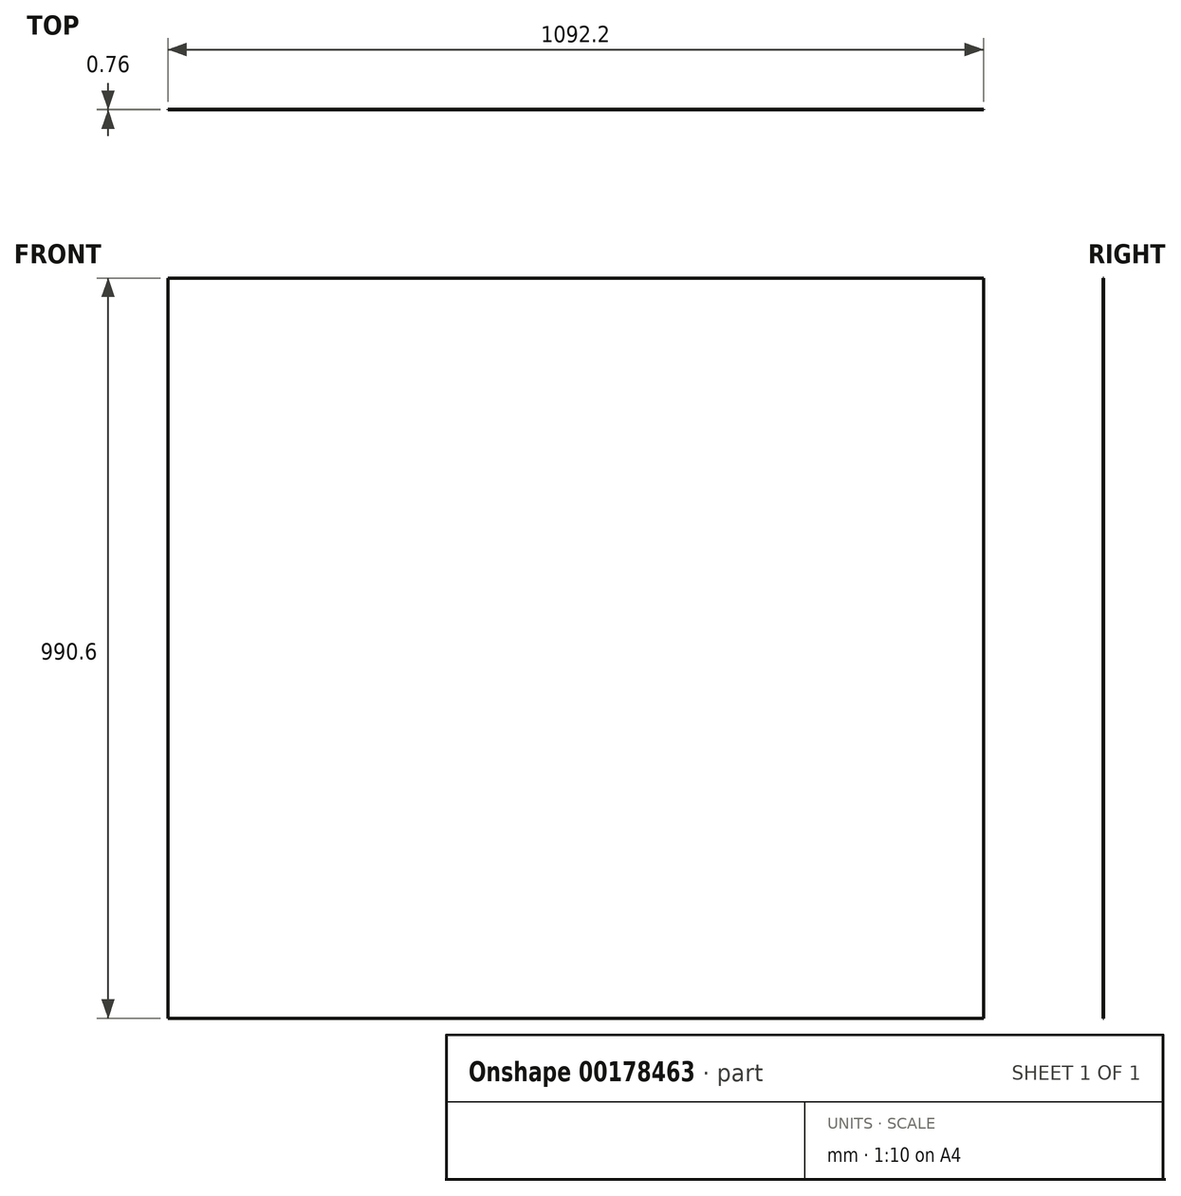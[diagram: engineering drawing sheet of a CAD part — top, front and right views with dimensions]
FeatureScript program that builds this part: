
annotation { "Feature Type Name" : "Feature", "Feature Type Description" : "" }
export const myFeature = defineFeature(function(context is Context, id is Id, definition is map)
    precondition{}
    {
        {
            var Q0;
            Q0=qCreatedBy(makeId("Front.planeOp"),FACE);
            var sketch = newSketch(context, id + "F0", { "sketchPlane" : qUnion([Q0])});
            skLineSegment(sketch, "E0.bottom", {"start": v(546.1, 495.3) * mm, "end": v(-546.1, 495.3) * mm});
            skLineSegment(sketch, "E0.top", {"start": v(546.1, -495.3) * mm, "end": v(-546.1, -495.3) * mm});
            skLineSegment(sketch, "E0.left", {"start": v(546.1, 495.3) * mm, "end": v(546.1, -495.3) * mm});
            skLineSegment(sketch, "E0.right", {"start": v(-546.1, 495.3) * mm, "end": v(-546.1, -495.3) * mm});
            skPoint(sketch, "E0.middle", {"position": v(0, 0) * mm});
            skSolve(sketch);
        }
        {
            var Q0;
            Q0 = qSketchRegion(id + "F0", true);
            extrude(context, id + "F1", {"entities" : qUnion([Q0]), "depth" : 0.76 * mm});
        }
    });
